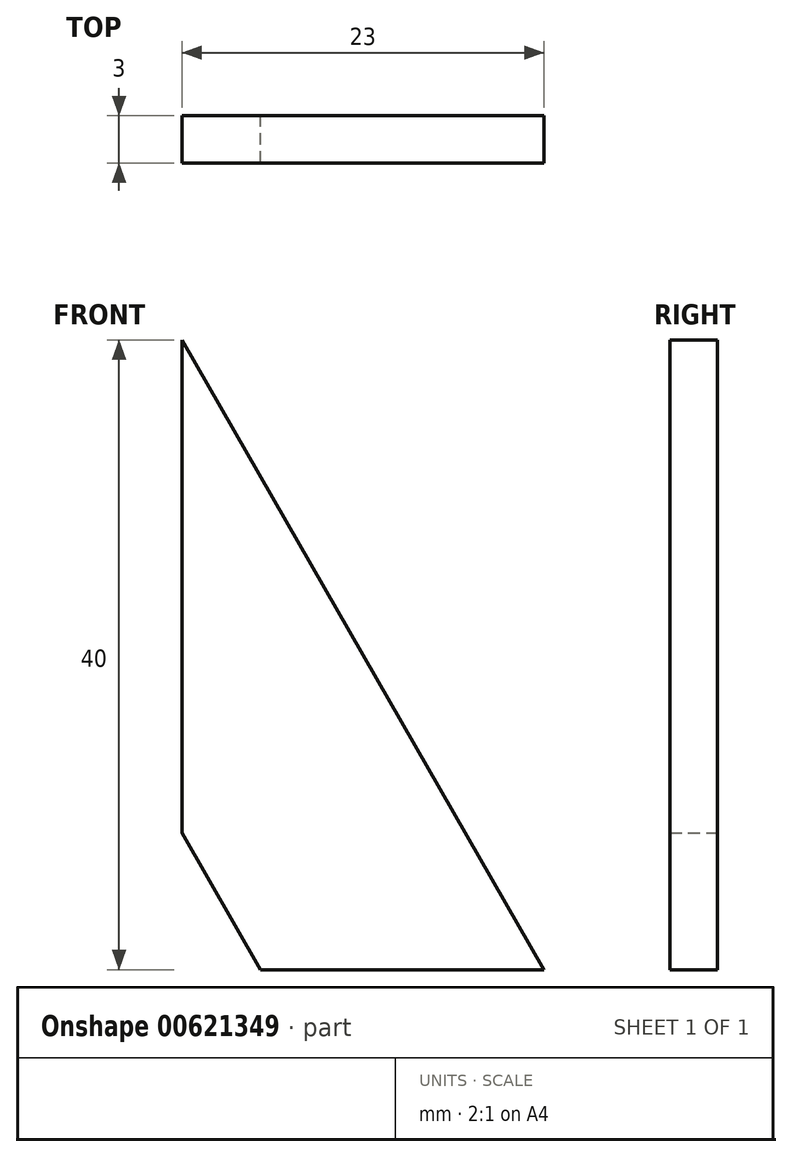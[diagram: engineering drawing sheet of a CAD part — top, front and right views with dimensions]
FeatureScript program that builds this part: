
annotation { "Feature Type Name" : "Feature", "Feature Type Description" : "" }
export const myFeature = defineFeature(function(context is Context, id is Id, definition is map)
    precondition{}
    {
        {
            var Q0;
            Q0=qCreatedBy(makeId("Front.planeOp"),FACE);
            var sketch = newSketch(context, id + "F0", { "sketchPlane" : qUnion([Q0])});
            skLineSegment(sketch, "E0", {"start": v(0, 0) * mm, "end": v(0, 31.3) * mm});
            skLineSegment(sketch, "E1", {"start": v(0, 31.3) * mm, "end": v(23, -8.7) * mm});
            skLineSegment(sketch, "E2", {"start": v(23, -8.7) * mm, "end": v(5, -8.7) * mm});
            skLineSegment(sketch, "E3", {"start": v(5, -8.7) * mm, "end": v(0, 0) * mm});
            skSolve(sketch);
        }
        {
            var Q0;
            Q0 = qSketchRegion(id + "F0", true);
            extrude(context, id + "F1", {"entities" : qUnion([Q0]), "depth" : 3 * mm, "offsetDistance" : 25 * mm});
        }
    });
